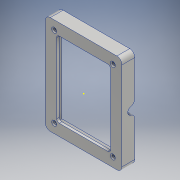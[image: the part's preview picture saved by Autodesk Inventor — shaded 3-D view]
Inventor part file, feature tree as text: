
AUTODESK INVENTOR PART (.ipt)
format: ipt  version: 2017 SP1 (Build 210196100, 196)  size: 158,208 bytes
history: native  units: mm
features: fillet x6, sketch x6, extrude x3, hole x2
ambient origin geometry x8: Origin, YZ Plane, XZ Plane, XY Plane, X Axis, Y Axis, Z Axis, Center Point
bodies: Solid1 (feature_tree)
feature tree (17):
  extrude  "Extrusion1"  Depth=77.0mm
  extrude  "Extrusion2"  Depth=54.0mm
  extrude  "Extrusion3"  Depth=8.0mm TaperAngle=0.0deg
  fillet  "Fillet1"  Radius=42.0mm
  sketch  "Sketch4"  dims[d9=59.0mm d10=7.0mm d11=0.0mm]
  hole  "Hole1"  [1 undecoded]
  hole  "Hole2"  [1 undecoded]
  fillet  "Fillet2"  Radius=2.0mm
  fillet  "Fillet3"  Radius=2.0mm
  fillet  "Fillet4"  Radius=2.0mm
  fillet  "Fillet5"  Radius=2.0mm
  fillet  "Fillet6"  [1 undecoded]
  sketch  "Sketch1"  dims[d0=60.0mm d1=77.0mm]
  sketch  "Sketch2"  dims[d2=10.0mm d3=0.0mm d4=54.0mm]
  sketch  "Sketch3"  dims[d5=71.0mm d6=8.0mm d7=0.0mm d8=42.0mm]
  sketch  "Sketch5"  dims[d12=4.0mm]
  sketch  "Sketch7"  dims[d13=2.459mm d14=6.0mm d15=4.0mm d16=2.0mm d17=90.0deg d18=8.8mm d19=20.594885mm d20=6.0mm d21=6.0mm d22=4.0mm d23=2.0mm d24=90.0deg d25=8.8mm d26=20.594885mm d27=4.0mm d28=2.0mm d29=2.0mm d30=2.0mm d31=2.0mm]
note: 3 required parameter values undecoded (feature->parameter linkage not recoverable at this tier; creation-order binding heuristic only, values carry confidence <= 0.55)
